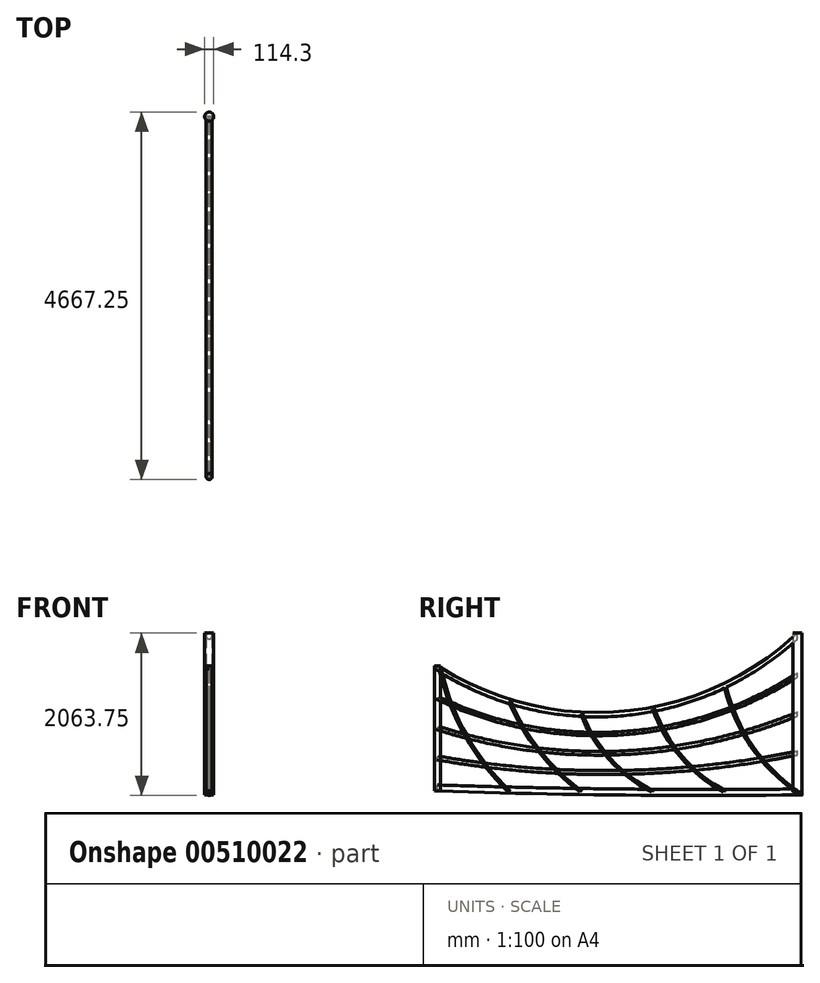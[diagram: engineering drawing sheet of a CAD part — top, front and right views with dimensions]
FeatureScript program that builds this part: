
annotation { "Feature Type Name" : "Feature", "Feature Type Description" : "" }
export const myFeature = defineFeature(function(context is Context, id is Id, definition is map)
    precondition{}
    {
        {
            var Q0;
            Q0=qCreatedBy(makeId("Right.planeOp"),FACE);
            var sketch = newSketch(context, id + "F0", { "sketchPlane" : qUnion([Q0])});
            skLineSegment(sketch, "E0.top", {"start": v(0, 1981.2) * mm, "end": v(-4572, 1981.2) * mm});
            skPoint(sketch, "E1", {"position": v(-2286, 990.6) * mm});
            skPoint(sketch, "E2", {"position": v(-4572, 1574.8) * mm});
            skPoint(sketch, "E3", {"position": v(-4572, 50.8) * mm});
            skArc(sketch, "E4", {"start": v(-4572, 1574.8) * mm, "mid": v(-2216.5, 996.13) * mm, "end": v(0, 1981.2) * mm});
            skArc(sketch, "E5", {"start": v(-4572, 50.8) * mm, "mid": v(-2286.28, 0) * mm, "end": v(0, 0) * mm});
            skPoint(sketch, "E6", {"position": v(-2286, 742.95) * mm});
            skPoint(sketch, "E7", {"position": v(-2286, 495.3) * mm});
            skPoint(sketch, "E8", {"position": v(-2286, 247.65) * mm});
            skPoint(sketch, "E9", {"position": v(0, 495.3) * mm});
            skPoint(sketch, "E10", {"position": v(0, 990.6) * mm});
            skPoint(sketch, "E11", {"position": v(0, 1485.9) * mm});
            skPoint(sketch, "E12", {"position": v(-4572, 431.8) * mm});
            skPoint(sketch, "E13", {"position": v(-4572, 812.8) * mm});
            skPoint(sketch, "E14", {"position": v(-4572, 1193.8) * mm});
            skArc(sketch, "E15", {"start": v(-4572, 1193.8) * mm, "mid": v(-2248, 745.22) * mm, "end": v(0, 1485.9) * mm});
            skArc(sketch, "E16", {"start": v(-4572, 812.8) * mm, "mid": v(-2270.22, 495.9) * mm, "end": v(0, 990.6) * mm});
            skArc(sketch, "E17", {"start": v(-4572, 431.8) * mm, "mid": v(-2283, 247.7) * mm, "end": v(0, 495.3) * mm});
            skSolve(sketch);
        }
        {
            var Q0;
            Q0=qCreatedBy(makeId("Front.planeOp"),FACE);
            var sketch = newSketch(context, id + "F1", { "sketchPlane" : qUnion([Q0])});
            skCircle(sketch, "E18", {"center": v(0, 495.3) * mm, "radius": 25.4 * mm});
            skCircle(sketch, "E19", {"center": v(0, 990.6) * mm, "radius": 25.4 * mm});
            skCircle(sketch, "E20", {"center": v(0, 1485.9) * mm, "radius": 25.4 * mm});
            skCircle(sketch, "E21", {"center": v(0, 2445.17) * mm, "radius": 40.75 * mm});
            skCircle(sketch, "E22", {"center": v(0, 1981.2) * mm, "radius": 38.1 * mm});
            skCircle(sketch, "E23", {"center": v(0, 0) * mm, "radius": 38.1 * mm});
            skSolve(sketch);
        }
        {
            var Q0;
            Q0=makeQuery(id+"F1.imprint","IMPRINT",FACE,{"disambiguationData":[TD([[makeQuery(id+"F1.imprint","IMPRINT",EDGE,{"derivedFrom":sQuery(id+"F1.wireOp",EDGE,"E18")}),1.0]])]});
            var Q1;
            Q1=sQuery(id+"F0.wireOp",EDGE,"E17");
            sweep(context, id + "F2", {"profiles" : qUnion([Q0]), "path" : qUnion([Q1])});
        }
        {
            var Q0;
            Q0=makeQuery(id+"F1.imprint","IMPRINT",FACE,{"disambiguationData":[TD([[makeQuery(id+"F1.imprint","IMPRINT",EDGE,{"derivedFrom":sQuery(id+"F1.wireOp",EDGE,"E23")}),1.0]])]});
            var Q1;
            Q1=sQuery(id+"F0.wireOp",EDGE,"E5");
            sweep(context, id + "F3", {"profiles" : qUnion([Q0]), "path" : qUnion([Q1])});
        }
        {
            var Q0;
            Q0=makeQuery(id+"F1.imprint","IMPRINT",FACE,{"disambiguationData":[TD([[makeQuery(id+"F1.imprint","IMPRINT",EDGE,{"derivedFrom":sQuery(id+"F1.wireOp",EDGE,"E19")}),1.0]])]});
            var Q1;
            Q1=sQuery(id+"F0.wireOp",EDGE,"E16");
            sweep(context, id + "F4", {"profiles" : qUnion([Q0]), "path" : qUnion([Q1])});
        }
        {
            var Q0;
            Q0=makeQuery(id+"F1.imprint","IMPRINT",FACE,{"disambiguationData":[TD([[makeQuery(id+"F1.imprint","IMPRINT",EDGE,{"derivedFrom":sQuery(id+"F1.wireOp",EDGE,"E20")}),1.0]])]});
            var Q1;
            Q1=sQuery(id+"F0.wireOp",EDGE,"E15");
            sweep(context, id + "F5", {"profiles" : qUnion([Q0]), "path" : qUnion([Q1])});
        }
        {
            var Q0;
            Q0=makeQuery(id+"F1.imprint","IMPRINT",FACE,{"disambiguationData":[TD([[makeQuery(id+"F1.imprint","IMPRINT",EDGE,{"derivedFrom":sQuery(id+"F1.wireOp",EDGE,"E22")}),1.0]])]});
            var Q1;
            Q1=sQuery(id+"F0.wireOp",EDGE,"E4");
            sweep(context, id + "F6", {"profiles" : qUnion([Q0]), "path" : qUnion([Q1])});
        }
        {
            var Q0;
            Q0=qCreatedBy(makeId("Top.planeOp"),FACE);
            var sketch = newSketch(context, id + "F7", { "sketchPlane" : qUnion([Q0])});
            skCircle(sketch, "E24", {"center": v(0, 0) * mm, "radius": 57.15 * mm});
            skSolve(sketch);
        }
        {
            var Q0;
            Q0=makeQuery(id+"F7.imprint","IMPRINT",FACE,{"disambiguationData":[TD([[makeQuery(id+"F7.imprint","IMPRINT",EDGE,{"derivedFrom":sQuery(id+"F7.wireOp",EDGE,"E24")}),1.0]])]});
            extrude(context, id + "F8", {"entities" : qUnion([Q0]), "depth" : 2019.3 * mm});
        }
        {
            var Q0;
            Q0=makeQuery(id+"F8.opExtrude","CAP_FACE",FACE,{"disambiguationData":[OSD([sQuery(id+"F7.wireOp",EDGE,"E24")])],"isStart":true});
            extrude(context, id + "F9", {"entities" : qUnion([Q0]), "depth" : 38.1 * mm});
        }
        {
            var Q0;
            Q0=qCreatedBy(makeId("Top.planeOp"),FACE);
            var sketch = newSketch(context, id + "F10", { "sketchPlane" : qUnion([Q0])});
            skCircle(sketch, "E25", {"center": v(0, -4572) * mm, "radius": 38.1 * mm});
            skSolve(sketch);
        }
        {
            var Q0;
            Q0=makeQuery(id+"F10.imprint","IMPRINT",FACE,{"disambiguationData":[TD([[makeQuery(id+"F10.imprint","IMPRINT",EDGE,{"derivedFrom":sQuery(id+"F10.wireOp",EDGE,"E25")}),1.0]])]});
            extrude(context, id + "F11", {"entities" : qUnion([Q0]), "depth" : 1600.2 * mm});
        }
        {
            var Q0;
            Q0=makeQuery(id+"F11.opExtrude","CAP_FACE",FACE,{"disambiguationData":[OSD([sQuery(id+"F10.wireOp",EDGE,"E25")])],"isStart":true});
            extrude(context, id + "F12", {"entities" : qUnion([Q0]), "operationType" : NewBodyOperationType.REMOVE, "oppositeDirection" : true, "depth" : 11.4 * mm});
        }
        {
            var Q0;
            Q0=qCreatedBy(makeId("Right.planeOp"),FACE);
            var sketch = newSketch(context, id + "F13", { "sketchPlane" : qUnion([Q0])});
            skLineSegment(sketch, "E26.bottom", {"start": v(0, 0) * mm, "end": v(-4572, 0) * mm});
            skLineSegment(sketch, "E26.top", {"start": v(0, 1624.47) * mm, "end": v(-4572, 1624.47) * mm});
            skLineSegment(sketch, "E26.left", {"start": v(0, 0) * mm, "end": v(0, 1624.47) * mm});
            skLineSegment(sketch, "E26.right", {"start": v(-4572, 0) * mm, "end": v(-4572, 1624.47) * mm});
            skPoint(sketch, "E27", {"position": v(-914.4, 0) * mm});
            skPoint(sketch, "E28", {"position": v(-1828.8, 0) * mm});
            skPoint(sketch, "E29", {"position": v(-2743.2, 0) * mm});
            skPoint(sketch, "E30", {"position": v(-3657.6, 0) * mm});
            skArc(sketch, "E31", {"start": v(-914.4, 1330.22) * mm, "mid": v(-579.78, 580.85) * mm, "end": v(0, 0) * mm});
            skArc(sketch, "E32", {"start": v(-1828.8, 1057.1) * mm, "mid": v(-1471.11, 442.48) * mm, "end": v(-914.4, 0) * mm});
            skArc(sketch, "E33", {"start": v(-2743.2, 994.42) * mm, "mid": v(-2379.02, 411.67) * mm, "end": v(-1828.8, 0) * mm});
            skArc(sketch, "E34", {"start": v(-3657.6, 1155.6) * mm, "mid": v(-3277.83, 516.53) * mm, "end": v(-2743.2, 0) * mm});
            skArc(sketch, "E35", {"start": v(-4532.03, 1534.83) * mm, "mid": v(-4205.6, 704.3) * mm, "end": v(-3657.6, 0) * mm});
            skArc(sketch, "E36.0", {"start": v(-926.74, 1327.23) * mm, "mid": v(-590.25, 573.65) * mm, "end": v(-7.21, -10.45) * mm});
            skArc(sketch, "E37.0", {"start": v(-902.06, 1333.21) * mm, "mid": v(-569.32, 588.04) * mm, "end": v(7.21, 10.45) * mm});
            skArc(sketch, "E38.0", {"start": v(-1840.77, 1052.86) * mm, "mid": v(-1480.72, 434.17) * mm, "end": v(-920.33, -11.23) * mm});
            skArc(sketch, "E39.0", {"start": v(-1816.83, 1061.35) * mm, "mid": v(-1461.5, 450.78) * mm, "end": v(-908.47, 11.23) * mm});
            skArc(sketch, "E40.0", {"start": v(-2755.02, 989.79) * mm, "mid": v(-2388.37, 403.08) * mm, "end": v(-1834.4, -11.4) * mm});
            skArc(sketch, "E41.0", {"start": v(-2731.38, 999.06) * mm, "mid": v(-2369.67, 420.27) * mm, "end": v(-1823.2, 11.4) * mm});
            skArc(sketch, "E42.0", {"start": v(-3669.28, 1150.63) * mm, "mid": v(-3287.79, 508.65) * mm, "end": v(-2750.73, -10.22) * mm});
            skArc(sketch, "E43.0", {"start": v(-3645.92, 1160.59) * mm, "mid": v(-3267.87, 524.42) * mm, "end": v(-2735.67, 10.22) * mm});
            skArc(sketch, "E44.0", {"start": v(-4544.4, 1531.92) * mm, "mid": v(-4216.64, 698) * mm, "end": v(-3666.4, -9.15) * mm});
            skArc(sketch, "E45.0", {"start": v(-4519.67, 1537.73) * mm, "mid": v(-4194.57, 710.58) * mm, "end": v(-3648.8, 9.15) * mm});
            skLineSegment(sketch, "E46", {"start": v(-926.74, 1327.23) * mm, "end": v(-902.06, 1333.21) * mm});
            skLineSegment(sketch, "E47", {"start": v(-1840.77, 1052.86) * mm, "end": v(-1816.83, 1061.35) * mm});
            skLineSegment(sketch, "E48", {"start": v(-2755.02, 989.79) * mm, "end": v(-2731.38, 999.06) * mm});
            skLineSegment(sketch, "E49", {"start": v(-3645.92, 1160.59) * mm, "end": v(-3669.28, 1150.63) * mm});
            skLineSegment(sketch, "E50", {"start": v(-4519.67, 1537.73) * mm, "end": v(-4544.4, 1531.92) * mm});
            skLineSegment(sketch, "E51", {"start": v(-3666.4, -9.15) * mm, "end": v(-3648.8, 9.15) * mm});
            skLineSegment(sketch, "E52", {"start": v(-2735.67, 10.22) * mm, "end": v(-2750.73, -10.22) * mm});
            skLineSegment(sketch, "E53", {"start": v(-1823.2, 11.4) * mm, "end": v(-1834.4, -11.4) * mm});
            skLineSegment(sketch, "E54", {"start": v(-920.33, -11.23) * mm, "end": v(-908.47, 11.23) * mm});
            skLineSegment(sketch, "E55", {"start": v(-7.21, -10.45) * mm, "end": v(7.21, 10.45) * mm});
            skSolve(sketch);
        }
        {
            var Q0;
            {var subQ0=sQuery(id+"F13.wireOp",EDGE,"E31");Q0=makeQuery(id+"F13.imprint","IMPRINT",FACE,{"disambiguationData":[TD([[makeQuery(id+"F13.imprint","IMPRINT",EDGE,{"derivedFrom":subQ0}),1.0]])]});}
            var Q1;
            {var subQ0=sQuery(id+"F13.wireOp",EDGE,"E31");Q1=makeQuery(id+"F13.imprint","IMPRINT",FACE,{"disambiguationData":[TD([[makeQuery(id+"F13.imprint","IMPRINT",EDGE,{"derivedFrom":subQ0}),-1.0]])]});}
            var Q2;
            {var subQ0=sQuery(id+"F13.wireOp",EDGE,"E32");Q2=makeQuery(id+"F13.imprint","IMPRINT",FACE,{"disambiguationData":[TD([[makeQuery(id+"F13.imprint","IMPRINT",EDGE,{"derivedFrom":subQ0}),1.0]])]});}
            var Q3;
            {var subQ0=sQuery(id+"F13.wireOp",EDGE,"E32");Q3=makeQuery(id+"F13.imprint","IMPRINT",FACE,{"disambiguationData":[TD([[makeQuery(id+"F13.imprint","IMPRINT",EDGE,{"derivedFrom":subQ0}),-1.0]])]});}
            var Q4;
            {var subQ0=sQuery(id+"F13.wireOp",EDGE,"E33");Q4=makeQuery(id+"F13.imprint","IMPRINT",FACE,{"disambiguationData":[TD([[makeQuery(id+"F13.imprint","IMPRINT",EDGE,{"derivedFrom":subQ0}),1.0]])]});}
            var Q5;
            {var subQ0=sQuery(id+"F13.wireOp",EDGE,"E33");Q5=makeQuery(id+"F13.imprint","IMPRINT",FACE,{"disambiguationData":[TD([[makeQuery(id+"F13.imprint","IMPRINT",EDGE,{"derivedFrom":subQ0}),-1.0]])]});}
            var Q6;
            {var subQ0=sQuery(id+"F13.wireOp",EDGE,"E34");Q6=makeQuery(id+"F13.imprint","IMPRINT",FACE,{"disambiguationData":[TD([[makeQuery(id+"F13.imprint","IMPRINT",EDGE,{"derivedFrom":subQ0}),1.0]])]});}
            var Q7;
            {var subQ0=sQuery(id+"F13.wireOp",EDGE,"E34");Q7=makeQuery(id+"F13.imprint","IMPRINT",FACE,{"disambiguationData":[TD([[makeQuery(id+"F13.imprint","IMPRINT",EDGE,{"derivedFrom":subQ0}),-1.0]])]});}
            var Q8;
            {var subQ0=sQuery(id+"F13.wireOp",EDGE,"E35");Q8=makeQuery(id+"F13.imprint","IMPRINT",FACE,{"disambiguationData":[TD([[makeQuery(id+"F13.imprint","IMPRINT",EDGE,{"derivedFrom":subQ0}),1.0]])]});}
            var Q9;
            {var subQ0=sQuery(id+"F13.wireOp",EDGE,"E35");Q9=makeQuery(id+"F13.imprint","IMPRINT",FACE,{"disambiguationData":[TD([[makeQuery(id+"F13.imprint","IMPRINT",EDGE,{"derivedFrom":subQ0}),-1.0]])]});}
            extrude(context, id + "F14", {"entities" : qUnion([Q0, Q1, Q2, Q3, Q4, Q5, Q6, Q7, Q8, Q9]), "endBound" : BoundingType.SYMMETRIC, "depth" : 25.4 * mm});
        }
    });
